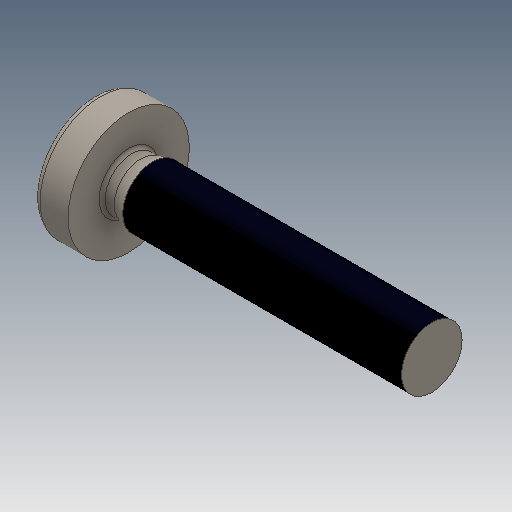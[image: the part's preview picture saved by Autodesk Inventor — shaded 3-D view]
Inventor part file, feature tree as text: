
AUTODESK INVENTOR PART (.ipt)
format: ipt  version: 2019 (Build 230136000, 136)  size: 195,072 bytes
history: native  units: mm
features: revolve x1
ambient origin geometry x8: Origin, YZ Plane, XZ Plane, XY Plane, X Axis, Y Axis, Z Axis, Center Point
bodies: Solid1 (feature_tree)
feature tree (1):
  revolve  "Revolve2"  [1 undecoded]
note: 1 required parameter value undecoded (feature->parameter linkage not recoverable at this tier; creation-order binding heuristic only, values carry confidence <= 0.55)
